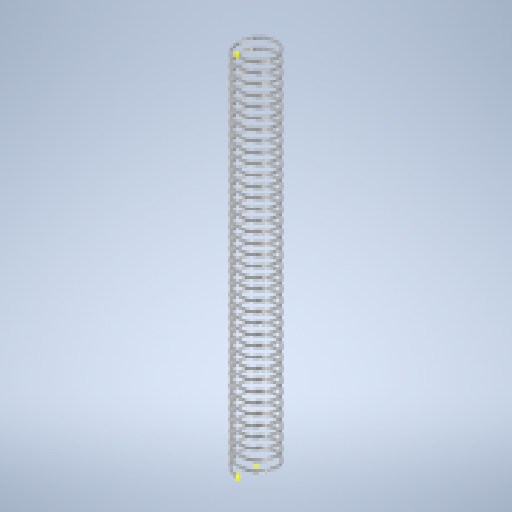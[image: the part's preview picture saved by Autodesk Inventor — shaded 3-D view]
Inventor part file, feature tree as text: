
AUTODESK INVENTOR PART (.ipt)
format: ipt  version: 2025.1 (Build 291241020, 241B)  size: 402,944 bytes
history: native  units: mm
features: sketch x3, plane x2, split x2, helix x1
ambient origin geometry x8: Origin, YZ Plane, XZ Plane, XY Plane, X Axis, Y Axis, Z Axis, Center Point
bodies: Solid1 (feature_tree)
feature tree (8):
  helix  "Coil1"  [1 undecoded]
  sketch  "Sketch2"  dims[d2=8.0mm d3=190.0mm d4=10.0mm d5=0.0mm d6=90.0deg d7=90.0deg d8=0.0mm d9=0.0mm]
  plane  "Work Plane1"
  sketch  "Sketch4"
  plane  "Work Plane2"
  split  "Split1"
  split  "Split2"
  sketch  "Sketch1"  dims[d1=9.4mm]
note: 1 required parameter value undecoded (feature->parameter linkage not recoverable at this tier; creation-order binding heuristic only, values carry confidence <= 0.55)
